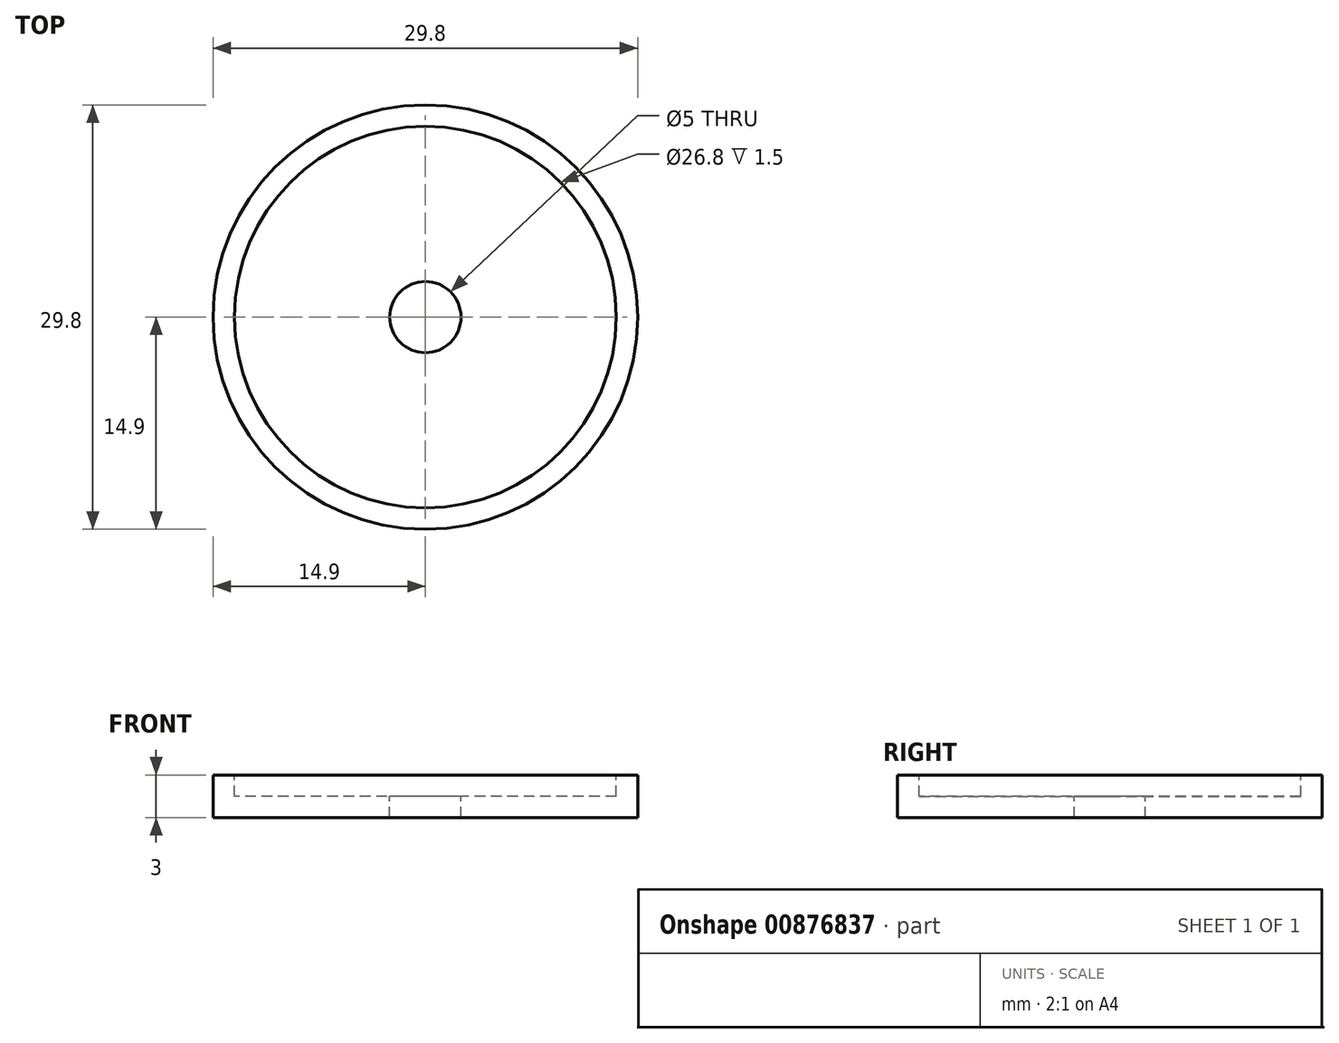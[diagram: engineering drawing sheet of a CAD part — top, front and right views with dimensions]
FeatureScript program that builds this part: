
annotation { "Feature Type Name" : "Feature", "Feature Type Description" : "" }
export const myFeature = defineFeature(function(context is Context, id is Id, definition is map)
    precondition{}
    {
        {
            var Q0;
            Q0=qCreatedBy(makeId("Top.planeOp"),FACE);
            var sketch = newSketch(context, id + "F0", { "sketchPlane" : qUnion([Q0])});
            skCircle(sketch, "E0", {"center": v(0, 0) * mm, "radius": 13.4 * mm});
            skCircle(sketch, "E1", {"center": v(0, 0) * mm, "radius": 14.9 * mm});
            skCircle(sketch, "E2", {"center": v(0, 0) * mm, "radius": 2.5 * mm});
            skSolve(sketch);
        }
        {
            var Q0;
            Q0=makeQuery(id+"F0.imprint","IMPRINT",FACE,{"disambiguationData":[TD([[makeQuery(id+"F0.imprint","IMPRINT",EDGE,{"derivedFrom":sQuery(id+"F0.wireOp",EDGE,"E0")}),-1.0]])]});
            var Q1;
            Q1=makeQuery(id+"F0.imprint","IMPRINT",FACE,{"disambiguationData":[TD([[makeQuery(id+"F0.imprint","IMPRINT",EDGE,{"derivedFrom":sQuery(id+"F0.wireOp",EDGE,"E0")}),1.0]])]});
            extrude(context, id + "F1", {"entities" : qUnion([Q0, Q1]), "oppositeDirection" : true, "depth" : 3 * mm, "offsetDistance" : 25 * mm});
        }
        {
            var Q0;
            Q0=makeQuery(id+"F0.imprint","IMPRINT",FACE,{"disambiguationData":[TD([[makeQuery(id+"F0.imprint","IMPRINT",EDGE,{"derivedFrom":sQuery(id+"F0.wireOp",EDGE,"E0")}),1.0]])]});
            extrude(context, id + "F2", {"entities" : qUnion([Q0]), "operationType" : NewBodyOperationType.REMOVE, "oppositeDirection" : true, "depth" : 1.5 * mm, "offsetDistance" : 25 * mm});
        }
    });
